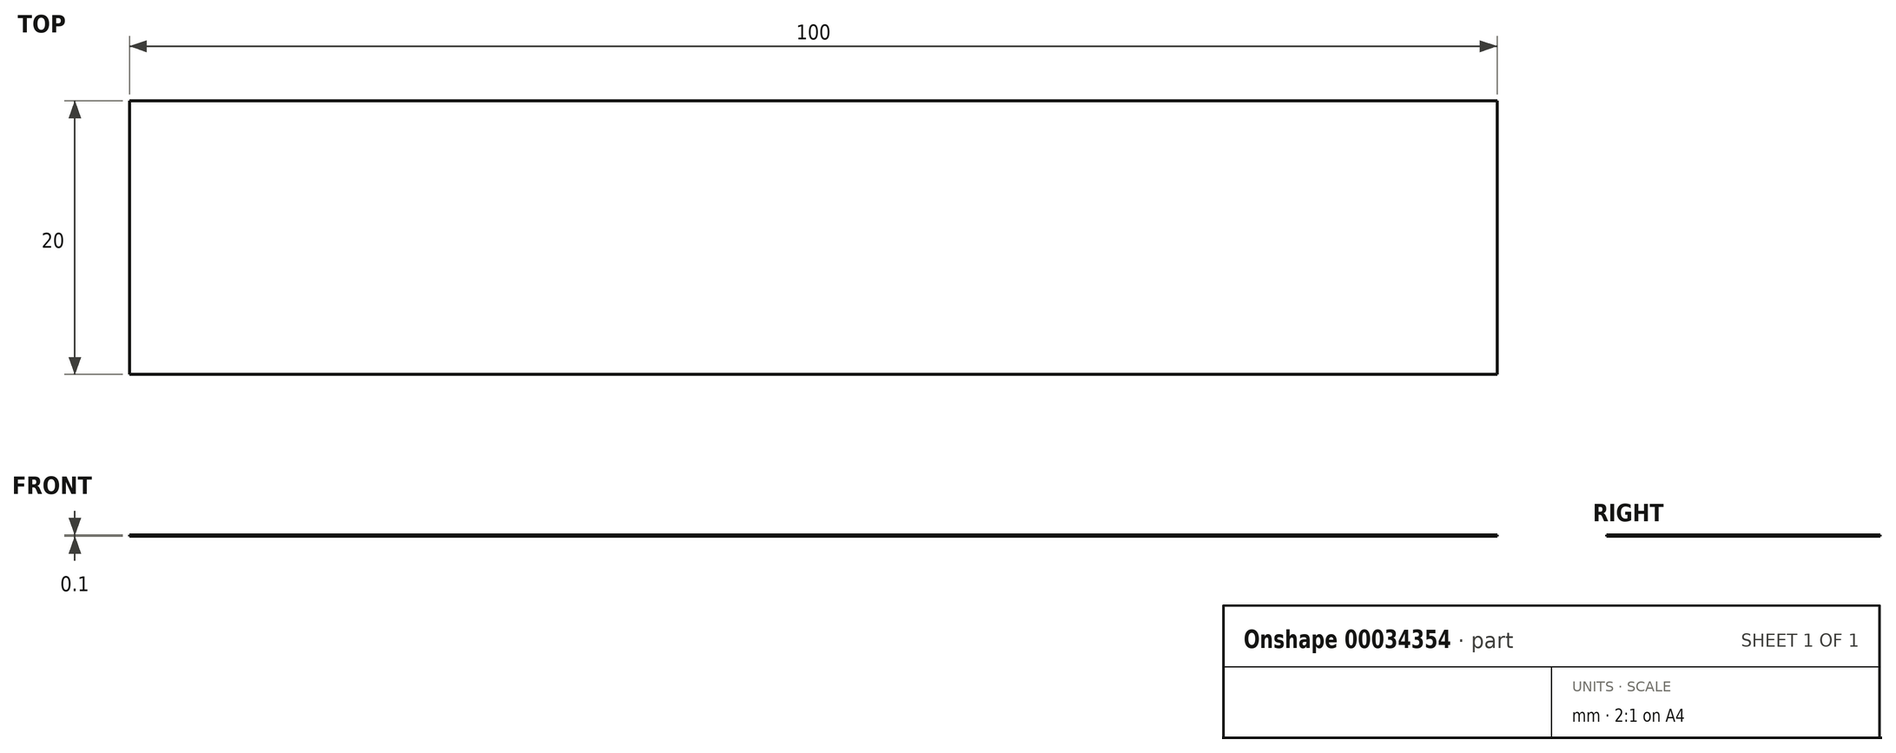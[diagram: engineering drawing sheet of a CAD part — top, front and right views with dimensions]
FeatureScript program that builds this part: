
annotation { "Feature Type Name" : "Feature", "Feature Type Description" : "" }
export const myFeature = defineFeature(function(context is Context, id is Id, definition is map)
    precondition{}
    {
        {
            var Q0;
            Q0=qCreatedBy(makeId("Top.planeOp"),FACE);
            var sketch = newSketch(context, id + "F0", { "sketchPlane" : qUnion([Q0])});
            skLineSegment(sketch, "E0.rect.bottom", {"start": v(50, -10) * mm, "end": v(-50, -10) * mm});
            skLineSegment(sketch, "E0.rect.top", {"start": v(50, 10) * mm, "end": v(-50, 10) * mm});
            skLineSegment(sketch, "E0.rect.left", {"start": v(50, -10) * mm, "end": v(50, 10) * mm});
            skLineSegment(sketch, "E0.rect.right", {"start": v(-50, -10) * mm, "end": v(-50, 10) * mm});
            skPoint(sketch, "E0.rect.middle", {"position": v(0, 0) * mm});
            skSolve(sketch);
        }
        {
            var Q0;
            Q0 = qSketchRegion(id + "F0", true);
            extrude(context, id + "F1", {"entities" : qUnion([Q0]), "depth" : .1 * mm});
        }
    });
